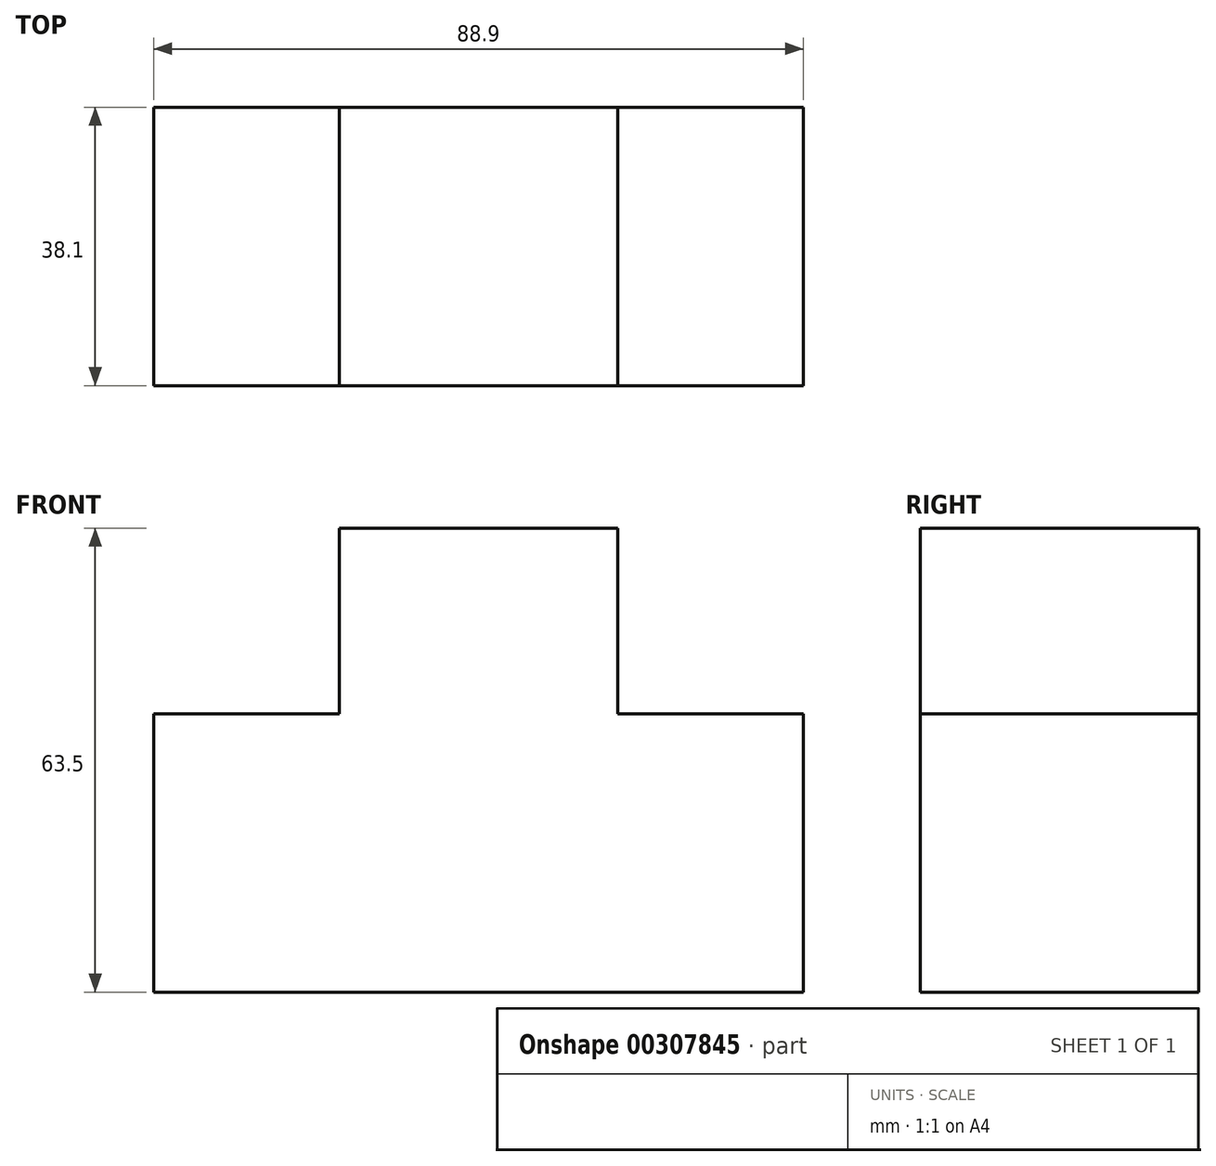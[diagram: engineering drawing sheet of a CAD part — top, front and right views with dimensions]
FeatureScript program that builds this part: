
annotation { "Feature Type Name" : "Feature", "Feature Type Description" : "" }
export const myFeature = defineFeature(function(context is Context, id is Id, definition is map)
    precondition{}
    {
        {
            var Q0;
            Q0=qCreatedBy(makeId("Front.planeOp"),FACE);
            var sketch = newSketch(context, id + "F0", { "sketchPlane" : qUnion([Q0])});
            skLineSegment(sketch, "E0", {"start": v(-43.15, -58.45) * mm, "end": v(45.75, -58.45) * mm});
            skLineSegment(sketch, "E1", {"start": v(45.75, -58.45) * mm, "end": v(45.75, -20.35) * mm});
            skLineSegment(sketch, "E2", {"start": v(45.75, -20.35) * mm, "end": v(20.35, -20.35) * mm});
            skLineSegment(sketch, "E3", {"start": v(20.35, -20.35) * mm, "end": v(20.35, 5.05) * mm});
            skLineSegment(sketch, "E4", {"start": v(20.35, 5.05) * mm, "end": v(-17.75, 5.05) * mm});
            skLineSegment(sketch, "E5", {"start": v(-17.75, 5.05) * mm, "end": v(-17.75, -20.35) * mm});
            skLineSegment(sketch, "E6", {"start": v(-17.75, -20.35) * mm, "end": v(-43.15, -20.35) * mm});
            skLineSegment(sketch, "E7", {"start": v(-43.15, -20.35) * mm, "end": v(-43.15, -58.45) * mm});
            skSolve(sketch);
        }
        {
            var Q0;
            Q0=makeQuery(id+"F0.imprint","IMPRINT",FACE,{"disambiguationData":[TD([[makeQuery(id+"F0.imprint","IMPRINT",EDGE,{"derivedFrom":sQuery(id+"F0.wireOp",EDGE,"E0")}),1.0]])]});
            extrude(context, id + "F1", {"entities" : qUnion([Q0]), "depth" : 38.1 * mm});
        }
    });
